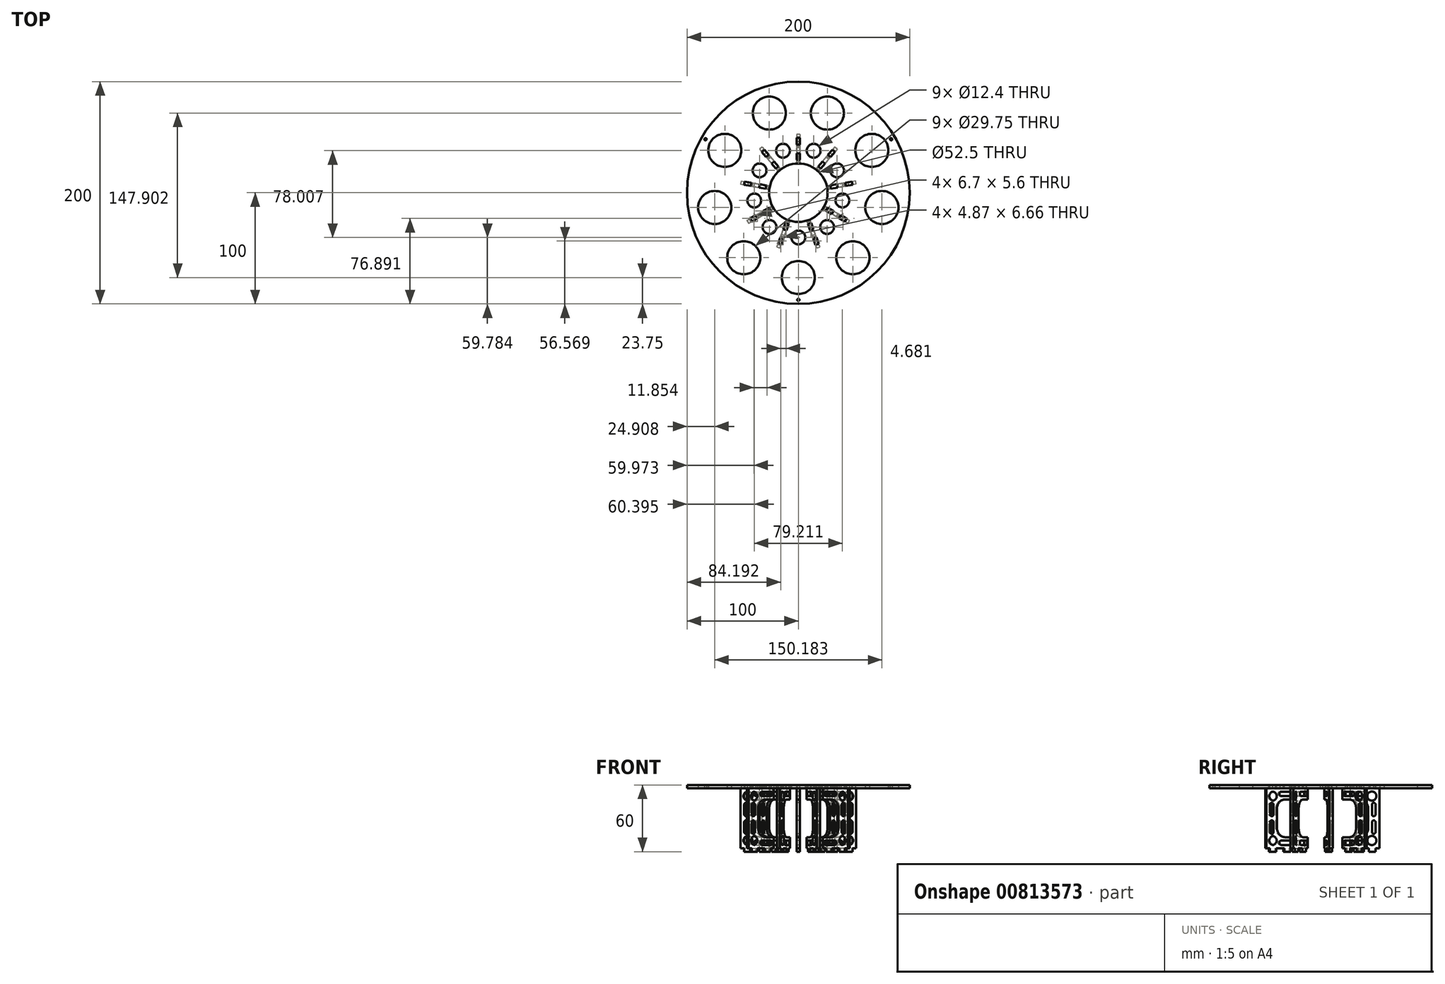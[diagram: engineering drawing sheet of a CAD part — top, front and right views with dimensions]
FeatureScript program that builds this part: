
annotation { "Feature Type Name" : "Feature", "Feature Type Description" : "" }
export const myFeature = defineFeature(function(context is Context, id is Id, definition is map)
    precondition{}
    {
        {
            assignVariable(context, id + "F0", {"name" : "flange_thickness", "anyValue" : 3});
        }
        {
            var Q0;
            Q0=qCreatedBy(makeId("Top.planeOp"),FACE);
            var sketch = newSketch(context, id + "F1", { "sketchPlane" : qUnion([Q0])});
            skLineSegment(sketch, "E0", {"start": v(0, 59.67) * mm, "end": v(0, 52.5) * mm, "construction": true});
            skLineSegment(sketch, "E1", {"start": v(-66.4, 0) * mm, "end": v(93.75, 0) * mm, "construction": true});
            skCircle(sketch, "E2", {"center": v(0, 0) * mm, "radius": 26.25 * mm});
            skCircle(sketch, "E3", {"center": v(0, 0) * mm, "radius": 52.5 * mm});
            skCircle(sketch, "E4", {"center": v(0, 0) * mm, "radius": 100 * mm});
            skLineSegment(sketch, "E5", {"start": v(-52.82, 0) * mm, "end": v(20.55, 0) * mm, "construction": true});
            skLineSegment(sketch, "E6.MirrorCS", {"start": v(1.5, 35.53) * mm, "end": v(1.5, 29.53) * mm});
            skLineSegment(sketch, "E7.MirrorCS", {"start": v(1.5, 49.22) * mm, "end": v(1.5, 43.22) * mm});
            skLineSegment(sketch, "E8.MirrorCS", {"start": v(-1.5, 49.22) * mm, "end": v(-1.5, 43.22) * mm});
            skLineSegment(sketch, "E9", {"start": v(1.5, 49.22) * mm, "end": v(-1.5, 49.22) * mm});
            skLineSegment(sketch, "E10", {"start": v(1.5, 43.22) * mm, "end": v(-1.5, 43.22) * mm});
            skLineSegment(sketch, "E11.MirrorCS", {"start": v(-1.5, 35.53) * mm, "end": v(-1.5, 29.53) * mm});
            skLineSegment(sketch, "E12", {"start": v(1.5, 29.53) * mm, "end": v(-1.5, 29.53) * mm});
            skLineSegment(sketch, "E13", {"start": v(1.5, 35.53) * mm, "end": v(-1.5, 35.53) * mm});
            skLineSegment(sketch, "E14", {"start": v(0, 52.5) * mm, "end": v(0, 26.25) * mm, "construction": true});
            skLineSegment(sketch, "E15", {"start": v(0, 26.25) * mm, "end": v(0, -100) * mm, "construction": true});
            skLineSegment(sketch, "E16.1.0", {"start": v(-21.69, 28.18) * mm, "end": v(-17.83, 23.59) * mm});
            skLineSegment(sketch, "E16.1.1", {"start": v(-23.99, 26.25) * mm, "end": v(-20.13, 21.66) * mm});
            skLineSegment(sketch, "E16.1.2", {"start": v(-17.83, 23.59) * mm, "end": v(-20.13, 21.66) * mm});
            skLineSegment(sketch, "E16.1.3", {"start": v(-21.69, 28.18) * mm, "end": v(-23.99, 26.25) * mm});
            skLineSegment(sketch, "E16.1.4", {"start": v(-26.63, 34.07) * mm, "end": v(-28.93, 32.14) * mm});
            skLineSegment(sketch, "E16.1.5", {"start": v(-30.49, 38.67) * mm, "end": v(-26.63, 34.07) * mm});
            skLineSegment(sketch, "E16.1.6", {"start": v(-32.79, 36.74) * mm, "end": v(-28.93, 32.14) * mm});
            skLineSegment(sketch, "E16.1.7", {"start": v(-30.49, 38.67) * mm, "end": v(-32.79, 36.74) * mm});
            skLineSegment(sketch, "E16.2.0", {"start": v(-34.73, 7.65) * mm, "end": v(-28.82, 6.6) * mm});
            skLineSegment(sketch, "E16.2.1", {"start": v(-35.25, 4.7) * mm, "end": v(-29.34, 3.65) * mm});
            skLineSegment(sketch, "E16.2.2", {"start": v(-28.82, 6.6) * mm, "end": v(-29.34, 3.65) * mm});
            skLineSegment(sketch, "E16.2.3", {"start": v(-34.73, 7.65) * mm, "end": v(-35.25, 4.7) * mm});
            skLineSegment(sketch, "E16.2.4", {"start": v(-42.3, 8.98) * mm, "end": v(-42.82, 6.03) * mm});
            skLineSegment(sketch, "E16.2.5", {"start": v(-48.21, 10.02) * mm, "end": v(-42.3, 8.98) * mm});
            skLineSegment(sketch, "E16.2.6", {"start": v(-48.73, 7.07) * mm, "end": v(-42.82, 6.03) * mm});
            skLineSegment(sketch, "E16.2.7", {"start": v(-48.21, 10.02) * mm, "end": v(-48.73, 7.07) * mm});
            skLineSegment(sketch, "E16.3.0", {"start": v(-31.52, -16.47) * mm, "end": v(-26.32, -13.47) * mm});
            skLineSegment(sketch, "E16.3.1", {"start": v(-30.02, -19.06) * mm, "end": v(-24.82, -16.06) * mm});
            skLineSegment(sketch, "E16.3.2", {"start": v(-26.32, -13.47) * mm, "end": v(-24.82, -16.06) * mm});
            skLineSegment(sketch, "E16.3.3", {"start": v(-31.52, -16.47) * mm, "end": v(-30.02, -19.06) * mm});
            skLineSegment(sketch, "E16.3.4", {"start": v(-38.18, -20.31) * mm, "end": v(-36.68, -22.9) * mm});
            skLineSegment(sketch, "E16.3.5", {"start": v(-43.37, -23.31) * mm, "end": v(-38.18, -20.31) * mm});
            skLineSegment(sketch, "E16.3.6", {"start": v(-41.87, -25.9) * mm, "end": v(-36.68, -22.9) * mm});
            skLineSegment(sketch, "E16.3.7", {"start": v(-43.37, -23.31) * mm, "end": v(-41.87, -25.9) * mm});
            skLineSegment(sketch, "E16.4.0", {"start": v(-13.56, -32.88) * mm, "end": v(-11.5, -27.24) * mm});
            skLineSegment(sketch, "E16.4.1", {"start": v(-10.74, -33.9) * mm, "end": v(-8.7, -28.26) * mm});
            skLineSegment(sketch, "E16.4.2", {"start": v(-11.5, -27.24) * mm, "end": v(-8.7, -28.26) * mm});
            skLineSegment(sketch, "E16.4.3", {"start": v(-13.56, -32.88) * mm, "end": v(-10.74, -33.9) * mm});
            skLineSegment(sketch, "E16.4.4", {"start": v(-16.2, -40.1) * mm, "end": v(-13.37, -41.13) * mm});
            skLineSegment(sketch, "E16.4.5", {"start": v(-18.24, -45.74) * mm, "end": v(-16.2, -40.1) * mm});
            skLineSegment(sketch, "E16.4.6", {"start": v(-15.42, -46.76) * mm, "end": v(-13.37, -41.13) * mm});
            skLineSegment(sketch, "E16.4.7", {"start": v(-18.24, -45.74) * mm, "end": v(-15.42, -46.76) * mm});
            skLineSegment(sketch, "E16.5.0", {"start": v(10.74, -33.9) * mm, "end": v(8.7, -28.26) * mm});
            skLineSegment(sketch, "E16.5.1", {"start": v(13.56, -32.88) * mm, "end": v(11.5, -27.24) * mm});
            skLineSegment(sketch, "E16.5.2", {"start": v(8.7, -28.26) * mm, "end": v(11.5, -27.24) * mm});
            skLineSegment(sketch, "E16.5.3", {"start": v(10.74, -33.9) * mm, "end": v(13.56, -32.88) * mm});
            skLineSegment(sketch, "E16.5.4", {"start": v(13.37, -41.13) * mm, "end": v(16.2, -40.1) * mm});
            skLineSegment(sketch, "E16.5.5", {"start": v(15.42, -46.76) * mm, "end": v(13.37, -41.13) * mm});
            skLineSegment(sketch, "E16.5.6", {"start": v(18.24, -45.74) * mm, "end": v(16.2, -40.1) * mm});
            skLineSegment(sketch, "E16.5.7", {"start": v(15.42, -46.76) * mm, "end": v(18.24, -45.74) * mm});
            skLineSegment(sketch, "E16.6.0", {"start": v(30.02, -19.06) * mm, "end": v(24.82, -16.06) * mm});
            skLineSegment(sketch, "E16.6.1", {"start": v(31.52, -16.47) * mm, "end": v(26.32, -13.47) * mm});
            skLineSegment(sketch, "E16.6.2", {"start": v(24.82, -16.06) * mm, "end": v(26.32, -13.47) * mm});
            skLineSegment(sketch, "E16.6.3", {"start": v(30.02, -19.06) * mm, "end": v(31.52, -16.47) * mm});
            skLineSegment(sketch, "E16.6.4", {"start": v(36.68, -22.9) * mm, "end": v(38.18, -20.31) * mm});
            skLineSegment(sketch, "E16.6.5", {"start": v(41.87, -25.9) * mm, "end": v(36.68, -22.9) * mm});
            skLineSegment(sketch, "E16.6.6", {"start": v(43.37, -23.31) * mm, "end": v(38.18, -20.31) * mm});
            skLineSegment(sketch, "E16.6.7", {"start": v(41.87, -25.9) * mm, "end": v(43.37, -23.31) * mm});
            skLineSegment(sketch, "E16.7.0", {"start": v(35.25, 4.7) * mm, "end": v(29.34, 3.65) * mm});
            skLineSegment(sketch, "E16.7.1", {"start": v(34.73, 7.65) * mm, "end": v(28.82, 6.6) * mm});
            skLineSegment(sketch, "E16.7.2", {"start": v(29.34, 3.65) * mm, "end": v(28.82, 6.6) * mm});
            skLineSegment(sketch, "E16.7.3", {"start": v(35.25, 4.7) * mm, "end": v(34.73, 7.65) * mm});
            skLineSegment(sketch, "E16.7.4", {"start": v(42.82, 6.03) * mm, "end": v(42.3, 8.98) * mm});
            skLineSegment(sketch, "E16.7.5", {"start": v(48.73, 7.07) * mm, "end": v(42.82, 6.03) * mm});
            skLineSegment(sketch, "E16.7.6", {"start": v(48.21, 10.02) * mm, "end": v(42.3, 8.98) * mm});
            skLineSegment(sketch, "E16.7.7", {"start": v(48.73, 7.07) * mm, "end": v(48.21, 10.02) * mm});
            skLineSegment(sketch, "E16.8.0", {"start": v(23.99, 26.25) * mm, "end": v(20.13, 21.66) * mm});
            skLineSegment(sketch, "E16.8.1", {"start": v(21.69, 28.18) * mm, "end": v(17.83, 23.59) * mm});
            skLineSegment(sketch, "E16.8.2", {"start": v(20.13, 21.66) * mm, "end": v(17.83, 23.59) * mm});
            skLineSegment(sketch, "E16.8.3", {"start": v(23.99, 26.25) * mm, "end": v(21.69, 28.18) * mm});
            skLineSegment(sketch, "E16.8.4", {"start": v(28.93, 32.14) * mm, "end": v(26.63, 34.07) * mm});
            skLineSegment(sketch, "E16.8.5", {"start": v(32.79, 36.74) * mm, "end": v(28.93, 32.14) * mm});
            skLineSegment(sketch, "E16.8.6", {"start": v(30.49, 38.67) * mm, "end": v(26.63, 34.07) * mm});
            skLineSegment(sketch, "E16.8.7", {"start": v(32.79, 36.74) * mm, "end": v(30.49, 38.67) * mm});
            skCircle(sketch, "E17", {"center": v(0, -40.22) * mm, "radius": 6.2 * mm});
            skCircle(sketch, "E18", {"center": v(0, -76.25) * mm, "radius": 14.87 * mm});
            skCircle(sketch, "E19.1.0", {"center": v(49.01, -58.41) * mm, "radius": 14.87 * mm});
            skCircle(sketch, "E19.1.1", {"center": v(25.85, -30.8) * mm, "radius": 6.2 * mm});
            skCircle(sketch, "E19.2.0", {"center": v(75.1, -13.24) * mm, "radius": 14.87 * mm});
            skCircle(sketch, "E19.2.1", {"center": v(39.6, -6.98) * mm, "radius": 6.2 * mm});
            skCircle(sketch, "E19.3.0", {"center": v(66.03, 38.13) * mm, "radius": 14.87 * mm});
            skCircle(sketch, "E19.3.1", {"center": v(34.83, 20.1) * mm, "radius": 6.2 * mm});
            skCircle(sketch, "E19.4.0", {"center": v(26.08, 71.65) * mm, "radius": 14.87 * mm});
            skCircle(sketch, "E19.4.1", {"center": v(13.75, 37.8) * mm, "radius": 6.2 * mm});
            skCircle(sketch, "E19.5.0", {"center": v(-26.08, 71.65) * mm, "radius": 14.87 * mm});
            skCircle(sketch, "E19.5.1", {"center": v(-13.75, 37.8) * mm, "radius": 6.2 * mm});
            skCircle(sketch, "E19.6.0", {"center": v(-66.03, 38.13) * mm, "radius": 14.87 * mm});
            skCircle(sketch, "E19.6.1", {"center": v(-34.83, 20.1) * mm, "radius": 6.2 * mm});
            skCircle(sketch, "E19.7.0", {"center": v(-75.1, -13.24) * mm, "radius": 14.87 * mm});
            skCircle(sketch, "E19.7.1", {"center": v(-39.6, -6.98) * mm, "radius": 6.2 * mm});
            skCircle(sketch, "E19.8.0", {"center": v(-49.01, -58.41) * mm, "radius": 14.87 * mm});
            skCircle(sketch, "E19.8.1", {"center": v(-25.85, -30.8) * mm, "radius": 6.2 * mm});
            skCircle(sketch, "E20", {"center": v(0, -96.3) * mm, "radius": 1 * mm});
            skCircle(sketch, "E21.1.0", {"center": v(83.4, 48.15) * mm, "radius": 1 * mm});
            skCircle(sketch, "E21.2.0", {"center": v(-83.4, 48.15) * mm, "radius": 1 * mm});
            skSolve(sketch);
        }
        {
            var Q0;
            Q0=qCreatedBy(makeId("Right.planeOp"),FACE);
            var sketch = newSketch(context, id + "F2", { "sketchPlane" : qUnion([Q0])});
            skLineSegment(sketch, "E22", {"start": v(52.5, 0) * mm, "end": v(52.5, -27) * mm});
            skLineSegment(sketch, "E23", {"start": v(26.25, 0) * mm, "end": v(26.25, -10) * mm});
            skLineSegment(sketch, "E24", {"start": v(0, 0) * mm, "end": v(0, -73.37) * mm, "construction": true});
            skLineSegment(sketch, "E25", {"start": v(52.5, 0) * mm, "end": v(49.22, 0) * mm});
            skLineSegment(sketch, "E26", {"start": v(43.22, 0) * mm, "end": v(35.53, 0) * mm});
            skLineSegment(sketch, "E27", {"start": v(29.53, 0) * mm, "end": v(26.25, 0) * mm});
            skLineSegment(sketch, "E28", {"start": v(49.22, 0) * mm, "end": v(49.22, 3) * mm});
            skLineSegment(sketch, "E29", {"start": v(49.22, 3) * mm, "end": v(43.22, 3) * mm});
            skLineSegment(sketch, "E30", {"start": v(43.22, 3) * mm, "end": v(43.22, 0) * mm});
            skLineSegment(sketch, "E31", {"start": v(35.53, 0) * mm, "end": v(35.53, 3) * mm});
            skLineSegment(sketch, "E32", {"start": v(35.53, 3) * mm, "end": v(29.53, 3) * mm});
            skLineSegment(sketch, "E33", {"start": v(29.53, 3) * mm, "end": v(29.53, 0) * mm});
            skLineSegment(sketch, "E34", {"start": v(26.25, -10) * mm, "end": v(34.5, -10) * mm});
            skLineSegment(sketch, "E35", {"start": v(42.5, -18) * mm, "end": v(42.5, -27) * mm});
            skLineSegment(sketch, "E36", {"start": v(42.5, -27) * mm, "end": v(52.5, -27) * mm});
            skPoint(sketch, "E37.visualSharp", {"position": v(42.5, -10) * mm});
            skArc(sketch, "E37.filletArc", {"start": v(42.5, -18) * mm, "mid": v(40.16, -12.34) * mm, "end": v(34.5, -10) * mm});
            skCircle(sketch, "E38", {"center": v(45.76, -7.04) * mm, "radius": 4.08 * mm});
            skLineSegment(sketch, "E39.left", {"start": v(49.1, -14.68) * mm, "end": v(49.1, -23.5) * mm});
            skLineSegment(sketch, "E39.right", {"start": v(45.9, -14.68) * mm, "end": v(45.9, -23.5) * mm});
            skArc(sketch, "E40", {"start": v(49.1, -14.68) * mm, "mid": v(47.5, -13.07) * mm, "end": v(45.9, -14.68) * mm});
            skArc(sketch, "E41", {"start": v(45.9, -23.5) * mm, "mid": v(47.5, -25.11) * mm, "end": v(49.1, -23.5) * mm});
            skLineSegment(sketch, "E42.left", {"start": v(38.35, -7) * mm, "end": v(29.53, -7) * mm});
            skLineSegment(sketch, "E42.right", {"start": v(38.35, -3) * mm, "end": v(29.53, -3) * mm});
            skArc(sketch, "E43", {"start": v(38.35, -7) * mm, "mid": v(40.34, -5) * mm, "end": v(38.35, -3) * mm});
            skArc(sketch, "E44", {"start": v(29.53, -3) * mm, "mid": v(27.54, -5) * mm, "end": v(29.53, -7) * mm});
            skLineSegment(sketch, "E45", {"start": v(51.53, -27) * mm, "end": v(23.27, -27) * mm, "construction": true});
            skLineSegment(sketch, "E46.MirrorCS", {"start": v(42.5, -36) * mm, "end": v(42.5, -27) * mm});
            skArc(sketch, "E47.MirrorCS", {"start": v(42.5, -36) * mm, "mid": v(40.16, -41.66) * mm, "end": v(34.5, -44) * mm});
            skLineSegment(sketch, "E48.MirrorCS", {"start": v(26.25, -44) * mm, "end": v(34.5, -44) * mm});
            skLineSegment(sketch, "E49.MirrorCS", {"start": v(26.25, -54) * mm, "end": v(26.25, -44) * mm});
            skLineSegment(sketch, "E50.MirrorCS", {"start": v(29.53, -54) * mm, "end": v(26.25, -54) * mm});
            skLineSegment(sketch, "E51.MirrorCS", {"start": v(29.53, -57) * mm, "end": v(29.53, -54) * mm});
            skLineSegment(sketch, "E52.MirrorCS", {"start": v(35.53, -57) * mm, "end": v(29.53, -57) * mm});
            skLineSegment(sketch, "E53.MirrorCS", {"start": v(35.53, -54) * mm, "end": v(35.53, -57) * mm});
            skLineSegment(sketch, "E54.MirrorCS", {"start": v(43.22, -54) * mm, "end": v(35.53, -54) * mm});
            skLineSegment(sketch, "E55.MirrorCS", {"start": v(43.22, -57) * mm, "end": v(43.22, -54) * mm});
            skLineSegment(sketch, "E56.MirrorCS", {"start": v(49.22, -57) * mm, "end": v(43.22, -57) * mm});
            skLineSegment(sketch, "E57.MirrorCS", {"start": v(49.22, -54) * mm, "end": v(49.22, -57) * mm});
            skLineSegment(sketch, "E58.MirrorCS", {"start": v(52.5, -54) * mm, "end": v(49.22, -54) * mm});
            skLineSegment(sketch, "E59.MirrorCS", {"start": v(52.5, -54) * mm, "end": v(52.5, -27) * mm});
            skCircle(sketch, "E60.MirrorC", {"center": v(45.76, -46.96) * mm, "radius": 4.08 * mm});
            skLineSegment(sketch, "E61.MirrorCS", {"start": v(49.1, -39.32) * mm, "end": v(49.1, -30.5) * mm});
            skArc(sketch, "E62.MirrorCS", {"start": v(49.1, -39.32) * mm, "mid": v(47.5, -40.93) * mm, "end": v(45.9, -39.32) * mm});
            skLineSegment(sketch, "E63.MirrorCS", {"start": v(45.9, -39.32) * mm, "end": v(45.9, -30.5) * mm});
            skArc(sketch, "E64.MirrorCS", {"start": v(45.9, -30.5) * mm, "mid": v(47.5, -28.89) * mm, "end": v(49.1, -30.5) * mm});
            skArc(sketch, "E65.MirrorCS", {"start": v(38.35, -47) * mm, "mid": v(40.34, -49) * mm, "end": v(38.35, -51) * mm});
            skLineSegment(sketch, "E66.MirrorCS", {"start": v(38.35, -47) * mm, "end": v(29.53, -47) * mm});
            skLineSegment(sketch, "E67.MirrorCS", {"start": v(38.35, -51) * mm, "end": v(29.53, -51) * mm});
            skArc(sketch, "E68.MirrorCS", {"start": v(29.53, -51) * mm, "mid": v(27.54, -49) * mm, "end": v(29.53, -47) * mm});
            skSolve(sketch);
        }
        {
            var Q0;
            Q0=makeQuery(id+"F1.imprint","IMPRINT",FACE,{"disambiguationData":[TD([[makeQuery(id+"F1.imprint","IMPRINT",EDGE,{"derivedFrom":sQuery(id+"F1.wireOp",EDGE,"E3")}),-1.0]])]});
            var Q1;
            Q1=makeQuery(id+"F1.imprint","IMPRINT",FACE,{"disambiguationData":[TD([[makeQuery(id+"F1.imprint","IMPRINT",EDGE,{"derivedFrom":sQuery(id+"F1.wireOp",EDGE,"E2")}),-1.0]])]});
            extrude(context, id + "F3", {"entities" : qUnion([Q0, Q1]), "depth" : (getVariable(context, 'flange_thickness')) * mm, "offsetDistance" : 25 * mm});
        }
        {
            var Q0;
            Q0=qCreatedBy(makeId("Front.planeOp"),FACE);
            var sketch = newSketch(context, id + "F4", { "sketchPlane" : qUnion([Q0])});
            skLineSegment(sketch, "E69", {"start": v(0, 0) * mm, "end": v(0, -63.74) * mm, "construction": true});
            skSolve(sketch);
        }
        {
            var Q0;
            Q0=makeQuery(id+"F2.imprint","IMPRINT",FACE,{"disambiguationData":[TD([[makeQuery(id+"F2.imprint","IMPRINT",EDGE,{"derivedFrom":sQuery(id+"F2.wireOp",EDGE,"E36")}),-1.0]])]});
            var Q1;
            Q1=makeQuery(id+"F2.imprint","IMPRINT",FACE,{"disambiguationData":[TD([[makeQuery(id+"F2.imprint","IMPRINT",EDGE,{"derivedFrom":sQuery(id+"F2.wireOp",EDGE,"E22")}),-1.0]])]});
            extrude(context, id + "F5", {"entities" : qUnion([Q0, Q1]), "endBound" : BoundingType.SYMMETRIC, "depth" : (getVariable(context, 'flange_thickness')) * mm, "offsetDistance" : 25 * mm});
        }
        {
            var Q0;
            Q0=makeQuery(id+"F5.opExtrude","SWEPT_BODY",BODY,{"disambiguationData":[OSD([sQuery(id+"F2.wireOp",EDGE,"E22"),sQuery(id+"F2.wireOp",EDGE,"E23"),sQuery(id+"F2.wireOp",EDGE,"E25"),sQuery(id+"F2.wireOp",EDGE,"E26"),sQuery(id+"F2.wireOp",EDGE,"E27"),sQuery(id+"F2.wireOp",EDGE,"E28"),sQuery(id+"F2.wireOp",EDGE,"E29"),sQuery(id+"F2.wireOp",EDGE,"E30"),sQuery(id+"F2.wireOp",EDGE,"E31"),sQuery(id+"F2.wireOp",EDGE,"E32"),sQuery(id+"F2.wireOp",EDGE,"E33"),sQuery(id+"F2.wireOp",EDGE,"E34"),sQuery(id+"F2.wireOp",EDGE,"E35"),sQuery(id+"F2.wireOp",EDGE,"E37.filletArc"),sQuery(id+"F2.wireOp",EDGE,"E38"),sQuery(id+"F2.wireOp",EDGE,"E39.left"),sQuery(id+"F2.wireOp",EDGE,"E39.right"),sQuery(id+"F2.wireOp",EDGE,"E40"),sQuery(id+"F2.wireOp",EDGE,"E41"),sQuery(id+"F2.wireOp",EDGE,"E42.left"),sQuery(id+"F2.wireOp",EDGE,"E42.right"),sQuery(id+"F2.wireOp",EDGE,"E43"),sQuery(id+"F2.wireOp",EDGE,"E44"),sQuery(id+"F2.wireOp",EDGE,"E46.MirrorCS"),sQuery(id+"F2.wireOp",EDGE,"E47.MirrorCS"),sQuery(id+"F2.wireOp",EDGE,"E48.MirrorCS"),sQuery(id+"F2.wireOp",EDGE,"E49.MirrorCS"),sQuery(id+"F2.wireOp",EDGE,"E50.MirrorCS"),sQuery(id+"F2.wireOp",EDGE,"E51.MirrorCS"),sQuery(id+"F2.wireOp",EDGE,"E52.MirrorCS"),sQuery(id+"F2.wireOp",EDGE,"E53.MirrorCS"),sQuery(id+"F2.wireOp",EDGE,"E54.MirrorCS"),sQuery(id+"F2.wireOp",EDGE,"E55.MirrorCS"),sQuery(id+"F2.wireOp",EDGE,"E56.MirrorCS"),sQuery(id+"F2.wireOp",EDGE,"E57.MirrorCS"),sQuery(id+"F2.wireOp",EDGE,"E58.MirrorCS"),sQuery(id+"F2.wireOp",EDGE,"E59.MirrorCS"),sQuery(id+"F2.wireOp",EDGE,"E60.MirrorC"),sQuery(id+"F2.wireOp",EDGE,"E61.MirrorCS"),sQuery(id+"F2.wireOp",EDGE,"E62.MirrorCS"),sQuery(id+"F2.wireOp",EDGE,"E63.MirrorCS"),sQuery(id+"F2.wireOp",EDGE,"E64.MirrorCS"),sQuery(id+"F2.wireOp",EDGE,"E65.MirrorCS"),sQuery(id+"F2.wireOp",EDGE,"E66.MirrorCS"),sQuery(id+"F2.wireOp",EDGE,"E67.MirrorCS"),sQuery(id+"F2.wireOp",EDGE,"E68.MirrorCS")])]});
            var Q1;
            Q1=sQuery(id+"F4.wireOp",EDGE,"E69");
            circularPattern(context, id + "F6", {"entities" : qUnion([Q0]), "axis" : qUnion([Q1]), "angle" : 360 * degree, "instanceCount" : 9, "equalSpace" : true});
        }
    });
